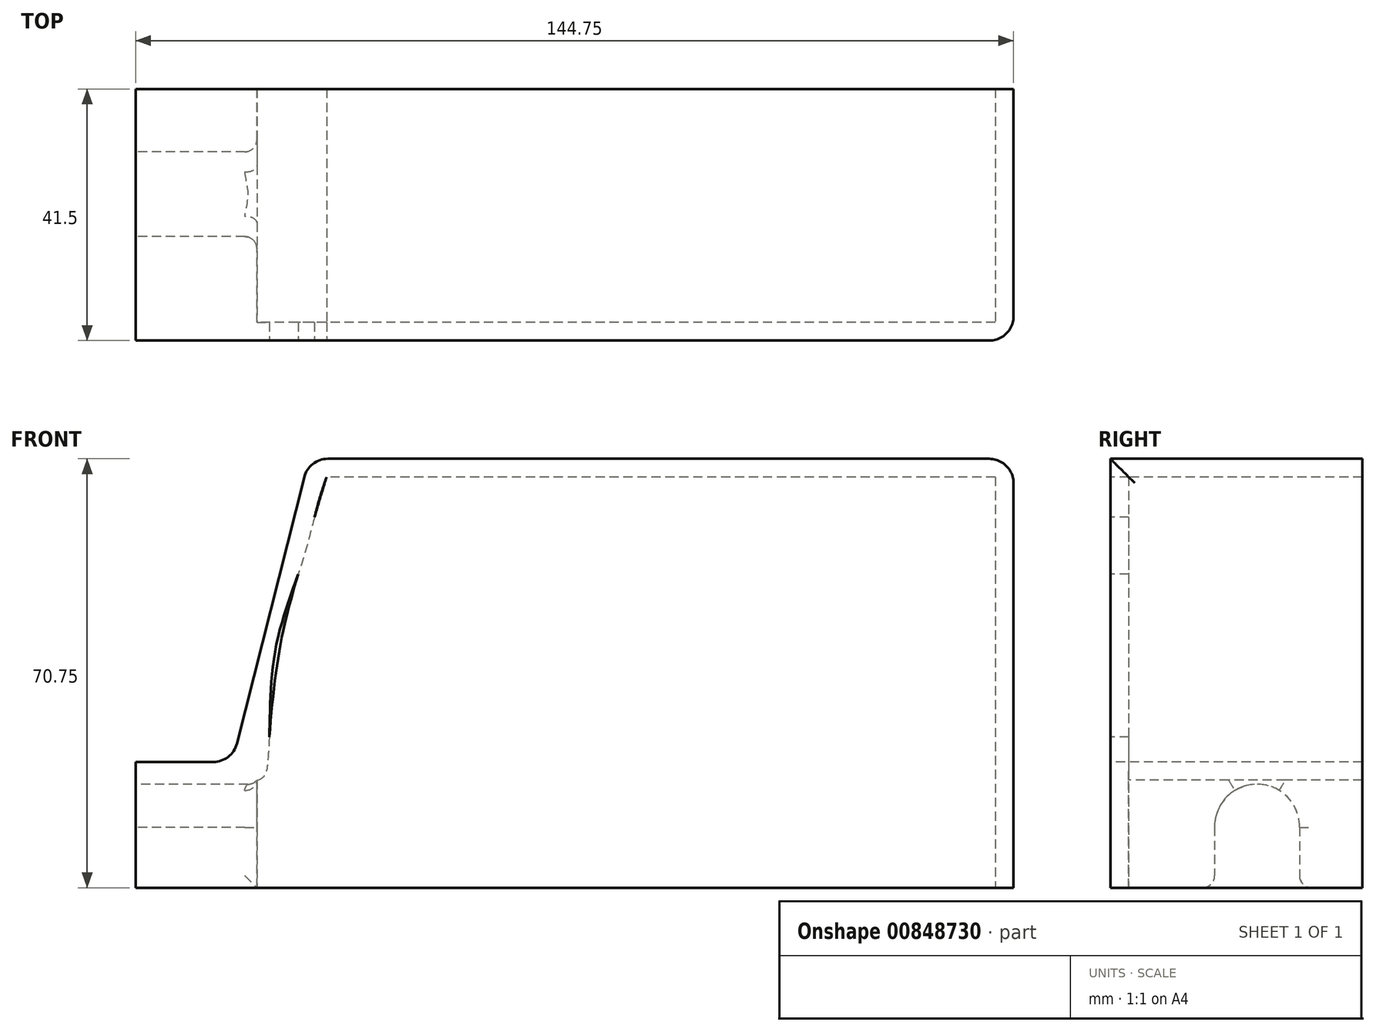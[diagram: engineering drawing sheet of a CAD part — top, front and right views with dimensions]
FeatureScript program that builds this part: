
annotation { "Feature Type Name" : "Feature", "Feature Type Description" : "" }
export const myFeature = defineFeature(function(context is Context, id is Id, definition is map)
    precondition{}
    {
        {
            var Q0;
            Q0=qCreatedBy(makeId("Front.planeOp"),FACE);
            var sketch = newSketch(context, id + "F0", { "sketchPlane" : qUnion([Q0])});
            skLineSegment(sketch, "E0", {"start": v(110.25, 24.1) * mm, "end": v(0, 24.1) * mm});
            skFitSpline(sketch, "E1", {"points": [v(0, 24.1) * mm, v(-4.07, 10.26) * mm, v(-7.71, -4.08) * mm, v(-10, -25.9) * mm], "startDerivative": vector(-13.66, -42.75) * mm, "endDerivative": vector(-4.48, -59.85) * mm});
            skLineSegment(sketch, "E2", {"start": v(110.26, -43.65) * mm, "end": v(-28.5, -43.65) * mm});
            skLineSegment(sketch, "E3", {"start": v(-28.5, -43.65) * mm, "end": v(-28.5, -25.9) * mm});
            skLineSegment(sketch, "E4", {"start": v(-28.5, -25.9) * mm, "end": v(-10, -25.9) * mm});
            skLineSegment(sketch, "E5", {"start": v(110.25, 24.1) * mm, "end": v(110.26, -43.65) * mm});
            skSolve(sketch);
        }
        {
            var Q0;
            Q0=qSketchRegion(id+"F0",true);
            extrude(context, id + "F1", {"entities" : qUnion([Q0]), "oppositeDirection" : true, "depth" : 3 * mm, "offsetDistance" : 25 * mm});
        }
        {
            var Q0;
            Q0=makeQuery(id+"F0.imprint","IMPRINT",FACE,{"disambiguationData":[TD([[makeQuery(id+"F0.imprint","IMPRINT",EDGE,{"derivedFrom":sQuery(id+"F0.wireOp",EDGE,"E0")}),1.0]])]});
            var Q1;
            Q1=qBodyType(qCreatedBy(id+"Fs2WI9H54nxdFtR_1",EDGE),BodyType.WIRE);
            cPlane(context, id + "F2", {"entities" : qUnion([Q0, Q1]), "cplaneType" : CPlaneType.OFFSET, "offset" : 0 * mm, "width" : 150 * mm, "height" : 150 * mm});
        }
        {
            var Q0;
            Q0=qCreatedBy(id+"F2.planeOp",FACE);
            var sketch = newSketch(context, id + "F3", { "sketchPlane" : qUnion([Q0])});
            skLineSegment(sketch, "E6.0.0", {"start": v(-28.5, -25.9) * mm, "end": v(-28.5, -43.65) * mm});
            skLineSegment(sketch, "E6.0.2", {"start": v(110.26, -43.65) * mm, "end": v(110.25, 24.1) * mm});
            skLineSegment(sketch, "E6.0.3", {"start": v(110.25, 24.1) * mm, "end": v(0, 24.1) * mm});
            skFitSpline(sketch, "E6.0.4", {"points": [v(0, 24.1) * mm, v(-1.4, 19.7) * mm, v(-4.08, 9.94) * mm, v(-8.4, -4.13) * mm, v(-9.43, -18.32) * mm, v(-10, -25.9) * mm]});
            skLineSegment(sketch, "E6.0.5", {"start": v(-10, -25.9) * mm, "end": v(-28.5, -25.9) * mm});
            skLineSegment(sketch, "E7", {"start": v(-28.5, -43.65) * mm, "end": v(-31.5, -43.65) * mm});
            skLineSegment(sketch, "E8", {"start": v(-31.5, -43.65) * mm, "end": v(-31.5, -22.9) * mm});
            skLineSegment(sketch, "E9", {"start": v(-31.5, -22.9) * mm, "end": v(-15.56, -22.9) * mm});
            skLineSegment(sketch, "E10", {"start": v(-15.56, -22.9) * mm, "end": v(-2.92, 27.1) * mm});
            skLineSegment(sketch, "E11", {"start": v(-2.92, 27.1) * mm, "end": v(113.26, 27.1) * mm});
            skLineSegment(sketch, "E12", {"start": v(113.26, 27.1) * mm, "end": v(113.26, -43.65) * mm});
            skLineSegment(sketch, "E13", {"start": v(113.26, -43.65) * mm, "end": v(110.26, -43.65) * mm});
            skSolve(sketch);
        }
        {
            var Q0;
            Q0=qSketchRegion(id+"F3",true);
            extrude(context, id + "F4", {"entities" : qUnion([Q0]), "oppositeDirection" : true, "depth" : 41.5 * mm, "offsetDistance" : 25 * mm});
        }
        {
            var Q0;
            Q0=makeQuery(id+"F4.opExtrude","SWEPT_FACE",FACE,{"disambiguationData":[OSD([sQuery(id+"F3.wireOp",EDGE,"E8")])]});
            cPlane(context, id + "F5", {"entities" : qUnion([Q0]), "cplaneType" : CPlaneType.OFFSET, "offset" : 0 * mm, "width" : 150 * mm, "height" : 150 * mm});
        }
        {
            var Q0;
            Q0=qCreatedBy(id+"F5.planeOp",FACE);
            var sketch = newSketch(context, id + "F6", { "sketchPlane" : qUnion([Q0])});
            skArc(sketch, "E14", {"start": v(-17.15, -33.62) * mm, "mid": v(-24.19, -26.58) * mm, "end": v(-31.15, -33.7) * mm});
            skLineSegment(sketch, "E15", {"start": v(-17.15, -33.62) * mm, "end": v(-17.15, -53.22) * mm});
            skLineSegment(sketch, "E16", {"start": v(-31.15, -33.46) * mm, "end": v(-31.15, -53.02) * mm});
            skLineSegment(sketch, "E17", {"start": v(-31.15, -53.02) * mm, "end": v(-17.15, -53.22) * mm});
            skSolve(sketch);
        }
        {
            var Q0;
            Q0=qSketchRegion(id+"F6",true);
            extrude(context, id + "F7", {"entities" : qUnion([Q0]), "operationType" : NewBodyOperationType.REMOVE, "oppositeDirection" : true, "depth" : 25 * mm, "offsetDistance" : 25 * mm});
        }
        {
            var Q0;
            Q0=makeQuery(id+"F4.opExtrude","SWEPT_FACE",FACE,{"disambiguationData":[OSD([sQuery(id+"F3.wireOp",EDGE,"E6.0.0")])]});
            cPlane(context, id + "F8", {"entities" : qUnion([Q0]), "cplaneType" : CPlaneType.OFFSET, "offset" : 0 * mm, "width" : 150 * mm, "height" : 150 * mm});
        }
        {
            var Q0;
            Q0=qCreatedBy(id+"F8.planeOp",FACE);
            var sketch = newSketch(context, id + "F9", { "sketchPlane" : qUnion([Q0])});
            skArc(sketch, "E18.0.0", {"start": v(17.15, -33.62) * mm, "mid": v(24.19, -26.58) * mm, "end": v(31.15, -33.7) * mm});
            skLineSegment(sketch, "E18.0.1", {"start": v(31.15, -33.7) * mm, "end": v(31.15, -43.65) * mm});
            skLineSegment(sketch, "E18.0.2", {"start": v(31.15, -43.65) * mm, "end": v(41.5, -43.65) * mm});
            skLineSegment(sketch, "E18.0.3", {"start": v(41.5, -43.65) * mm, "end": v(41.5, -25.9) * mm});
            skLineSegment(sketch, "E18.0.4", {"start": v(41.5, -25.9) * mm, "end": v(0, -25.9) * mm});
            skLineSegment(sketch, "E18.0.5", {"start": v(0, -25.9) * mm, "end": v(0, -43.65) * mm});
            skLineSegment(sketch, "E18.0.6", {"start": v(0, -43.65) * mm, "end": v(17.15, -43.65) * mm});
            skLineSegment(sketch, "E18.0.7", {"start": v(17.15, -43.65) * mm, "end": v(17.15, -33.62) * mm});
            skSolve(sketch);
        }
        {
            var Q0;
            Q0=qSketchRegion(id+"F9",true);
            extrude(context, id + "F10", {"entities" : qUnion([Q0]), "operationType" : NewBodyOperationType.ADD, "depth" : 17 * mm, "offsetDistance" : 25 * mm});
        }
        {
            var Q0;
            Q0=makeQuery(id+"F4.opExtrude","SWEPT_EDGE",EDGE,{"disambiguationData":[OSD([sQuery(id+"F3.wireOp",EDGE,"E11"),sQuery(id+"F3.wireOp",EDGE,"E12")])]});
            var Q1;
            Q1=makeQuery(id+"F4.opExtrude","SWEPT_EDGE",EDGE,{"disambiguationData":[OSD([sQuery(id+"F3.wireOp",EDGE,"E10"),sQuery(id+"F3.wireOp",EDGE,"E11")])]});
            var Q2;
            Q2=makeQuery(id+"F4.opExtrude","SWEPT_EDGE",EDGE,{"disambiguationData":[OSD([sQuery(id+"F3.wireOp",EDGE,"E9"),sQuery(id+"F3.wireOp",EDGE,"E10")])]});
            var Q3;
            Q3=makeQuery(id+"F4.opExtrude","CAP_EDGE",EDGE,{"disambiguationData":[OSD([sQuery(id+"F3.wireOp",EDGE,"E12")])],"isStart":true});
            fillet(context, id + "F11", {"entities" : qUnion([Q0, Q1, Q2, Q3]), "radius" : 4 * mm, "tangentPropagation" : true, "allowEdgeOverflow" : false});
        }
        {
            var Q0;
            Q0=makeQuery(id+"F4.opExtrude","SWEPT_EDGE",EDGE,{"disambiguationData":[OSD([sQuery(id+"F3.wireOp",EDGE,"E6.0.4"),sQuery(id+"F3.wireOp",EDGE,"E6.0.5")])]});
            var Q1;
            Q1=makeQuery(id+"F10.opExtrude","CAP_EDGE",EDGE,{"disambiguationData":[OSD([sQuery(id+"F9.wireOp",EDGE,"E18.0.0")])],"isStart":false});
            var Q2;
            Q2=makeQuery(id+"F10.opExtrude","CAP_EDGE",EDGE,{"disambiguationData":[OSD([sQuery(id+"F9.wireOp",EDGE,"E18.0.7")])],"isStart":false});
            var Q3;
            Q3=makeQuery(id+"F10.opExtrude","CAP_EDGE",EDGE,{"disambiguationData":[OSD([sQuery(id+"F9.wireOp",EDGE,"E18.0.1")])],"isStart":false});
            var Q4;
            Q4=makeQuery(id+"F7.boolean.opBoolean","COPY",EDGE,{"derivedFrom":makeQuery(id+"F7.opExtrude","CAP_EDGE",EDGE,{"disambiguationData":[OSD([sQuery(id+"F6.wireOp",EDGE,"E15")])],"isStart":true})});
            var Q5;
            Q5=makeQuery(id+"F7.boolean.opBoolean","COPY",EDGE,{"derivedFrom":makeQuery(id+"F7.opExtrude","CAP_EDGE",EDGE,{"disambiguationData":[OSD([sQuery(id+"F6.wireOp",EDGE,"E14")])],"isStart":true})});
            var Q6;
            Q6=makeQuery(id+"F7.boolean.opBoolean","COPY",EDGE,{"derivedFrom":makeQuery(id+"F7.opExtrude","CAP_EDGE",EDGE,{"disambiguationData":[OSD([sQuery(id+"F6.wireOp",EDGE,"E16")])],"isStart":true})});
            var Q7;
            Q7=makeQuery(id+"F10.opExtrude","SWEPT_EDGE",EDGE,{"disambiguationData":[OSD([sQuery(id+"F9.wireOp",EDGE,"E18.0.1"),sQuery(id+"F9.wireOp",EDGE,"E18.0.2")])]});
            var Q8;
            Q8=makeQuery(id+"F10.opExtrude","SWEPT_EDGE",EDGE,{"disambiguationData":[OSD([sQuery(id+"F9.wireOp",EDGE,"E18.0.6"),sQuery(id+"F9.wireOp",EDGE,"E18.0.7")])]});
            var Q9;
            Q9=makeQuery(id+"F7.boolean.opBoolean","INTERSECT",EDGE,{"derivedFrom":[makeQuery(id+"F4.opExtrude","SWEPT_FACE",FACE,{"disambiguationData":[OSD([sQuery(id+"F3.wireOp",EDGE,"E7")])]}),makeQuery(id+"F7.opExtrude","SWEPT_FACE",FACE,{"disambiguationData":[OSD([sQuery(id+"F6.wireOp",EDGE,"E15")])]})]});
            var Q10;
            Q10=makeQuery(id+"F7.boolean.opBoolean","INTERSECT",EDGE,{"derivedFrom":[makeQuery(id+"F4.opExtrude","SWEPT_FACE",FACE,{"disambiguationData":[OSD([sQuery(id+"F3.wireOp",EDGE,"E7")])]}),makeQuery(id+"F7.opExtrude","SWEPT_FACE",FACE,{"disambiguationData":[OSD([sQuery(id+"F6.wireOp",EDGE,"E16")])]})]});
            var Q11;
            Q11=makeQuery(id+"F7JnHAPWnQUtylZ_4.opExtrude","CAP_EDGE",EDGE,{"disambiguationData":[OSD([sQuery(id+"FFYtz8uIwUbJl5E_4.wireOp",EDGE,"zmeNoECs-TdjU-asCO-wawC-rF3gaWaOfeAG")])],"isStart":true});
            fillet(context, id + "F12", {"entities" : qUnion([Q0, Q1, Q2, Q3, Q4, Q5, Q6, Q7, Q8, Q9, Q10, Q11]), "radius" : 2 * mm, "tangentPropagation" : true, "allowEdgeOverflow" : false});
        }
    });
